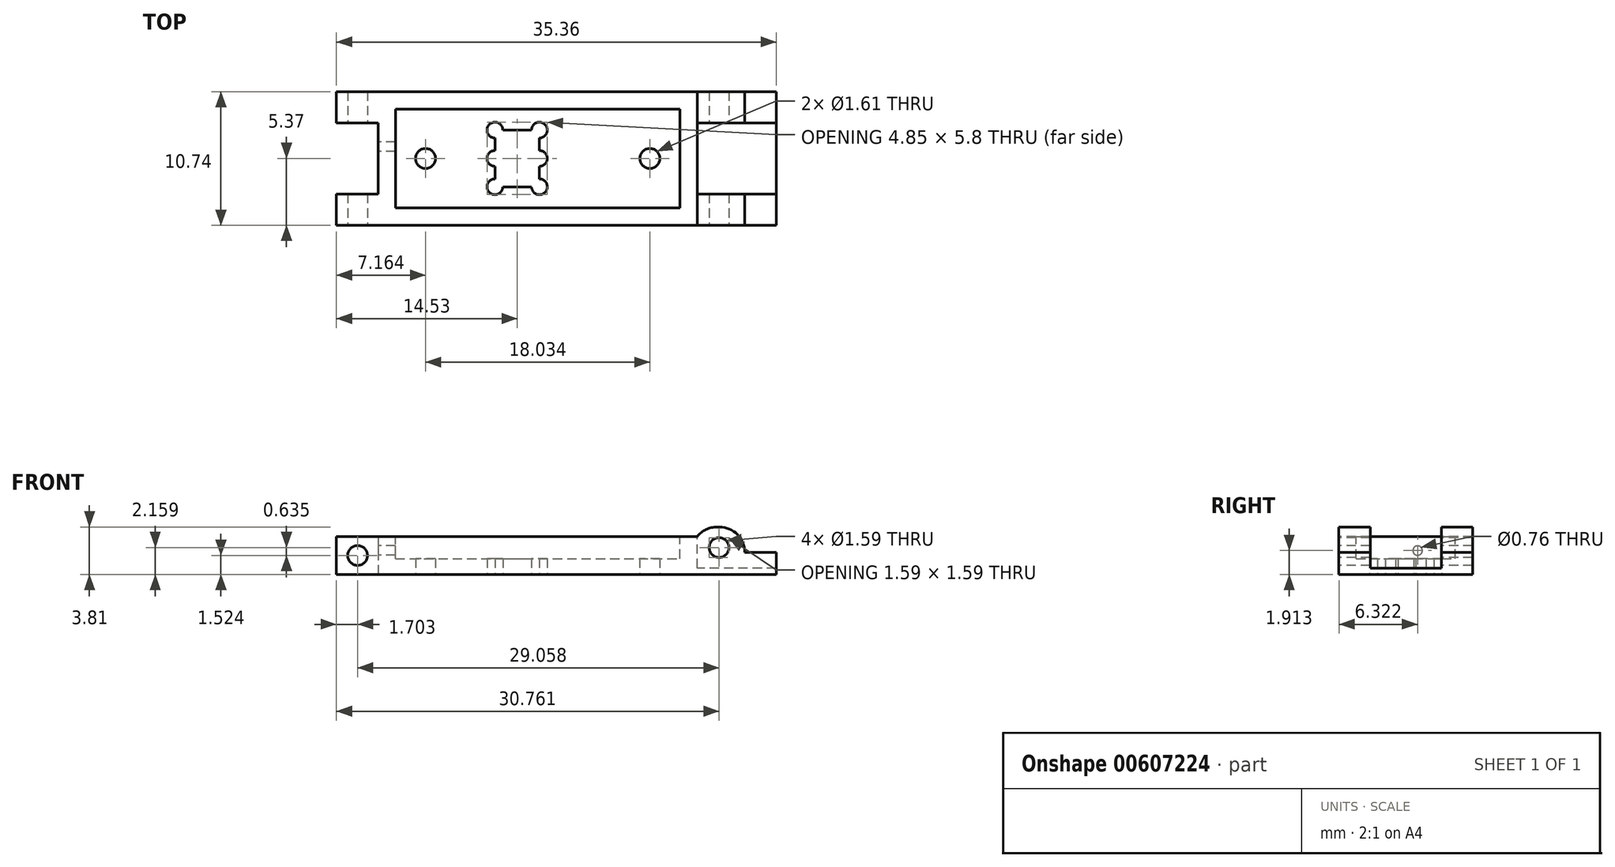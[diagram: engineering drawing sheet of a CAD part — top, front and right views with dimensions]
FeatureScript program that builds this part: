
annotation { "Feature Type Name" : "Feature", "Feature Type Description" : "" }
export const myFeature = defineFeature(function(context is Context, id is Id, definition is map)
    precondition{}
    {
        {
            var Q0;
            Q0=qCreatedBy(makeId("Top.planeOp"),FACE);
            var sketch = newSketch(context, id + "F0", { "sketchPlane" : qUnion([Q0])});
            skLineSegment(sketch, "E0.bottom", {"start": v(1.48, 1.88) * mm, "end": v(-1.47, 1.88) * mm, "construction": true});
            skLineSegment(sketch, "E0.top", {"start": v(1.48, -1.88) * mm, "end": v(-1.47, -1.88) * mm, "construction": true});
            skLineSegment(sketch, "E0.left", {"start": v(1.48, 1.88) * mm, "end": v(1.48, -1.88) * mm, "construction": true});
            skLineSegment(sketch, "E0.right", {"start": v(-1.47, 1.88) * mm, "end": v(-1.47, -1.88) * mm, "construction": true});
            skPoint(sketch, "E0.middle", {"position": v(0, 0) * mm});
            skLineSegment(sketch, "E1.bottom", {"start": v(1.79, 2.28) * mm, "end": v(-1.79, 2.28) * mm, "construction": true});
            skLineSegment(sketch, "E1.top", {"start": v(1.79, -2.28) * mm, "end": v(-1.79, -2.28) * mm, "construction": true});
            skLineSegment(sketch, "E2", {"start": v(-1.47, 1.88) * mm, "end": v(-1.79, 2.28) * mm, "construction": true});
            skLineSegment(sketch, "E3", {"start": v(1.79, -2.28) * mm, "end": v(1.48, -1.88) * mm, "construction": true});
            skLineSegment(sketch, "E4", {"start": v(-1.48, 1.88) * mm, "end": v(1.48, -1.88) * mm, "construction": true});
            skArc(sketch, "E5", {"start": v(-1.15, 2.28) * mm, "mid": v(-2.24, 2.73) * mm, "end": v(-1.79, 1.64) * mm});
            skArc(sketch, "E6", {"start": v(1.15, 2.28) * mm, "mid": v(2.24, 2.73) * mm, "end": v(1.79, 1.64) * mm});
            skArc(sketch, "E7", {"start": v(1.79, -1.64) * mm, "mid": v(2.24, -2.73) * mm, "end": v(1.15, -2.28) * mm});
            skArc(sketch, "E8", {"start": v(-1.15, -2.28) * mm, "mid": v(-2.24, -2.73) * mm, "end": v(-1.79, -1.64) * mm});
            skArc(sketch, "E9", {"start": v(-1.79, 0.64) * mm, "mid": v(-2.42, 0) * mm, "end": v(-1.79, -0.64) * mm});
            skArc(sketch, "E10", {"start": v(1.79, 0.64) * mm, "mid": v(2.42, 0) * mm, "end": v(1.79, -0.64) * mm});
            skLineSegment(sketch, "E11", {"start": v(-1.15, 2.28) * mm, "end": v(1.15, 2.28) * mm});
            skLineSegment(sketch, "E12", {"start": v(-1.79, 1.64) * mm, "end": v(-1.79, 0.64) * mm});
            skLineSegment(sketch, "E13", {"start": v(-1.79, -0.64) * mm, "end": v(-1.79, -1.64) * mm});
            skLineSegment(sketch, "E14", {"start": v(-1.15, -2.28) * mm, "end": v(1.15, -2.28) * mm});
            skLineSegment(sketch, "E15", {"start": v(1.79, -1.64) * mm, "end": v(1.79, -0.64) * mm});
            skLineSegment(sketch, "E16", {"start": v(1.79, 0.64) * mm, "end": v(1.79, 1.64) * mm});
            skLineSegment(sketch, "E17", {"start": v(-1.79, 2.28) * mm, "end": v(-1.79, -2.28) * mm, "construction": true});
            skLineSegment(sketch, "E18", {"start": v(1.79, 2.28) * mm, "end": v(1.79, -2.28) * mm, "construction": true});
            skLineSegment(sketch, "E19", {"start": v(20.83, 5.37) * mm, "end": v(20.83, -5.37) * mm});
            skCircle(sketch, "E20", {"center": v(-7.37, 0) * mm, "radius": 0.8 * mm});
            skCircle(sketch, "E21", {"center": v(10.67, 0) * mm, "radius": 0.8 * mm});
            skLineSegment(sketch, "E22.bottom", {"start": v(-11.18, 5.37) * mm, "end": v(-14.53, 5.37) * mm});
            skLineSegment(sketch, "E22.top", {"start": v(-11.18, 2.86) * mm, "end": v(-14.53, 2.86) * mm});
            skLineSegment(sketch, "E22.left", {"start": v(-11.18, 5.37) * mm, "end": v(-11.18, 2.86) * mm});
            skLineSegment(sketch, "E22.right", {"start": v(-14.53, 5.37) * mm, "end": v(-14.53, 2.86) * mm});
            skLineSegment(sketch, "E23.bottom", {"start": v(-11.18, -5.37) * mm, "end": v(-14.53, -5.37) * mm});
            skLineSegment(sketch, "E23.top", {"start": v(-11.18, -2.86) * mm, "end": v(-14.53, -2.86) * mm});
            skLineSegment(sketch, "E23.left", {"start": v(-11.18, -5.37) * mm, "end": v(-11.18, -2.86) * mm});
            skLineSegment(sketch, "E23.right", {"start": v(-14.53, -5.37) * mm, "end": v(-14.53, -2.86) * mm});
            skLineSegment(sketch, "E24.bottom", {"start": v(-11.18, -5.37) * mm, "end": v(14.48, -5.37) * mm});
            skLineSegment(sketch, "E24.top", {"start": v(-11.18, 5.37) * mm, "end": v(14.48, 5.37) * mm});
            skLineSegment(sketch, "E24.left", {"start": v(-11.18, -5.37) * mm, "end": v(-11.18, 5.37) * mm});
            skLineSegment(sketch, "E24.right", {"start": v(14.48, -5.37) * mm, "end": v(14.48, 5.37) * mm});
            skLineSegment(sketch, "E25.bottom", {"start": v(14.48, 5.37) * mm, "end": v(20.83, 5.37) * mm});
            skLineSegment(sketch, "E25.top", {"start": v(14.48, -5.37) * mm, "end": v(20.83, -5.37) * mm});
            skLineSegment(sketch, "E25.left", {"start": v(14.48, 5.37) * mm, "end": v(14.48, -5.37) * mm, "construction": true});
            skLineSegment(sketch, "E26", {"start": v(20.83, 0) * mm, "end": v(14.48, 0) * mm, "construction": true});
            skSolve(sketch);
        }
        {
            var Q0;
            Q0=makeQuery(id+"F0.imprint","IMPRINT",FACE,{"disambiguationData":[TD([[makeQuery(id+"F0.imprint","IMPRINT",EDGE,{"derivedFrom":sQuery(id+"F0.wireOp",EDGE,"E22.bottom")}),1.0]])]});
            var Q1;
            Q1=makeQuery(id+"F0.imprint","IMPRINT",FACE,{"disambiguationData":[TD([[makeQuery(id+"F0.imprint","IMPRINT",EDGE,{"derivedFrom":sQuery(id+"F0.wireOp",EDGE,"E23.bottom")}),-1.0]])]});
            var Q2;
            Q2=makeQuery(id+"F0.imprint","IMPRINT",FACE,{"disambiguationData":[TD([[makeQuery(id+"F0.imprint","IMPRINT",EDGE,{"derivedFrom":sQuery(id+"F0.wireOp",EDGE,"E5")}),-1.0]])]});
            var Q3;
            Q3=makeQuery(id+"F0.imprint","IMPRINT",FACE,{"disambiguationData":[TD([[makeQuery(id+"F0.imprint","IMPRINT",EDGE,{"derivedFrom":sQuery(id+"F0.wireOp",EDGE,"E24.right")}),-1.0]])]});
            extrude(context, id + "F1", {"entities" : qUnion([Q0, Q1, Q2, Q3]), "depth" : 3.05 * mm, "offsetDistance" : 25.4 * mm});
        }
        {
            var Q0;
            Q0=makeQuery(id+"F1.opExtrude","CAP_FACE",FACE,{"disambiguationData":[OSD([sQuery(id+"F0.wireOp",EDGE,"E5"),sQuery(id+"F0.wireOp",EDGE,"E6"),sQuery(id+"F0.wireOp",EDGE,"E7"),sQuery(id+"F0.wireOp",EDGE,"E8"),sQuery(id+"F0.wireOp",EDGE,"E9"),sQuery(id+"F0.wireOp",EDGE,"E10"),sQuery(id+"F0.wireOp",EDGE,"E11"),sQuery(id+"F0.wireOp",EDGE,"E12"),sQuery(id+"F0.wireOp",EDGE,"E13"),sQuery(id+"F0.wireOp",EDGE,"E14"),sQuery(id+"F0.wireOp",EDGE,"E15"),sQuery(id+"F0.wireOp",EDGE,"E16"),sQuery(id+"F0.wireOp",EDGE,"HfviohbY-Hr04-ZRmY-4y10-KckNNT6P6HvO.bottom"),sQuery(id+"F0.wireOp",EDGE,"HfviohbY-Hr04-ZRmY-4y10-KckNNT6P6HvO.top"),sQuery(id+"F0.wireOp",EDGE,"HfviohbY-Hr04-ZRmY-4y10-KckNNT6P6HvO.left"),sQuery(id+"F0.wireOp",EDGE,"HfviohbY-Hr04-ZRmY-4y10-KckNNT6P6HvO.right")])],"isStart":false});
            var sketch = newSketch(context, id + "F2", { "sketchPlane" : qUnion([Q0])});
            skLineSegment(sketch, "E27.bottom", {"start": v(20.83, 5.37) * mm, "end": v(18.29, 5.37) * mm});
            skLineSegment(sketch, "E27.top", {"start": v(20.83, -5.37) * mm, "end": v(18.29, -5.37) * mm});
            skLineSegment(sketch, "E27.left", {"start": v(20.83, 5.37) * mm, "end": v(20.83, -5.37) * mm});
            skLineSegment(sketch, "E27.right", {"start": v(18.29, 5.37) * mm, "end": v(18.29, -5.37) * mm});
            skCircle(sketch, "E28", {"center": v(-7.37, 0) * mm, "radius": 1.47 * mm, "construction": true});
            skCircle(sketch, "E29", {"center": v(10.67, 0) * mm, "radius": 1.47 * mm, "construction": true});
            skLineSegment(sketch, "E30", {"start": v(-11.18, 0) * mm, "end": v(-9.78, 0) * mm, "construction": true});
            skLineSegment(sketch, "E31", {"start": v(0, -5.37) * mm, "end": v(0, -3.98) * mm, "construction": true});
            skPoint(sketch, "E32.middle", {"position": v(0, 0) * mm});
            skLineSegment(sketch, "E33.bottom", {"start": v(-9.78, -3.98) * mm, "end": v(13.08, -3.98) * mm});
            skLineSegment(sketch, "E33.top", {"start": v(-9.78, 3.98) * mm, "end": v(13.08, 3.98) * mm});
            skLineSegment(sketch, "E33.left", {"start": v(-9.78, -3.98) * mm, "end": v(-9.78, 3.98) * mm});
            skLineSegment(sketch, "E33.right", {"start": v(13.08, -3.98) * mm, "end": v(13.08, 3.98) * mm});
            skLineSegment(sketch, "E34", {"start": v(-9.78, 0) * mm, "end": v(-8.84, 0) * mm, "construction": true});
            skLineSegment(sketch, "E35", {"start": v(13.08, 0) * mm, "end": v(12.14, 0) * mm, "construction": true});
            skSolve(sketch);
        }
        {
            var Q0;
            Q0=qSketchRegion(id+"F2",true);
            extrude(context, id + "F3", {"entities" : qUnion([Q0]), "operationType" : NewBodyOperationType.REMOVE, "oppositeDirection" : true, "depth" : 1.27 * mm, "offsetDistance" : 25.4 * mm});
        }
        {
            var Q0;
            Q0=makeQuery(id+"F1.opExtrude","CAP_FACE",FACE,{"disambiguationData":[OSD([sQuery(id+"F0.wireOp",EDGE,"E5"),sQuery(id+"F0.wireOp",EDGE,"E6"),sQuery(id+"F0.wireOp",EDGE,"E7"),sQuery(id+"F0.wireOp",EDGE,"E8"),sQuery(id+"F0.wireOp",EDGE,"E9"),sQuery(id+"F0.wireOp",EDGE,"E10"),sQuery(id+"F0.wireOp",EDGE,"E11"),sQuery(id+"F0.wireOp",EDGE,"E12"),sQuery(id+"F0.wireOp",EDGE,"E13"),sQuery(id+"F0.wireOp",EDGE,"E14"),sQuery(id+"F0.wireOp",EDGE,"E15"),sQuery(id+"F0.wireOp",EDGE,"E16"),sQuery(id+"F0.wireOp",EDGE,"HfviohbY-Hr04-ZRmY-4y10-KckNNT6P6HvO.bottom"),sQuery(id+"F0.wireOp",EDGE,"HfviohbY-Hr04-ZRmY-4y10-KckNNT6P6HvO.top"),sQuery(id+"F0.wireOp",EDGE,"HfviohbY-Hr04-ZRmY-4y10-KckNNT6P6HvO.left"),sQuery(id+"F0.wireOp",EDGE,"YcC6wYwr-SVXZ-vRu8-w98k-MYfRG6CX6vEh"),sQuery(id+"F0.wireOp",EDGE,"E19"),sQuery(id+"F0.wireOp",EDGE,"X6KMa0kz-Fo9u-lM4c-e0Po-d6rj0lJBtCXR"),sQuery(id+"F0.wireOp",EDGE,"E20"),sQuery(id+"F0.wireOp",EDGE,"E21"),sQuery(id+"F0.wireOp",EDGE,"E22.bottom"),sQuery(id+"F0.wireOp",EDGE,"E22.top"),sQuery(id+"F0.wireOp",EDGE,"E22.right"),sQuery(id+"F0.wireOp",EDGE,"E23.bottom"),sQuery(id+"F0.wireOp",EDGE,"E23.top"),sQuery(id+"F0.wireOp",EDGE,"E23.right")])],"isStart":false});
            var sketch = newSketch(context, id + "F4", { "sketchPlane" : qUnion([Q0])});
            skLineSegment(sketch, "E36.0", {"start": v(20.83, 5.37) * mm, "end": v(20.83, -5.37) * mm, "construction": true});
            skLineSegment(sketch, "E37.bottom", {"start": v(20.83, -2.86) * mm, "end": v(14.48, -2.86) * mm});
            skLineSegment(sketch, "E37.top", {"start": v(20.83, 2.86) * mm, "end": v(14.48, 2.86) * mm});
            skLineSegment(sketch, "E37.left", {"start": v(20.83, -2.86) * mm, "end": v(20.83, 2.86) * mm});
            skLineSegment(sketch, "E37.right", {"start": v(14.48, -2.86) * mm, "end": v(14.48, 2.86) * mm});
            skLineSegment(sketch, "E38", {"start": v(-11.18, 2.86) * mm, "end": v(14.48, 2.86) * mm, "construction": true});
            skLineSegment(sketch, "E39", {"start": v(14.48, -2.86) * mm, "end": v(-11.18, -2.86) * mm, "construction": true});
            skSolve(sketch);
        }
        {
            var Q0;
            Q0=qSketchRegion(id+"F4",true);
            extrude(context, id + "F5", {"entities" : qUnion([Q0]), "operationType" : NewBodyOperationType.REMOVE, "oppositeDirection" : true, "depth" : 2.54 * mm, "offsetDistance" : 25.4 * mm});
        }
        {
            var Q0;
            Q0=makeQuery(id+"F1.opExtrude","SWEPT_FACE",FACE,{"disambiguationData":[OSD([sQuery(id+"F0.wireOp",EDGE,"HfviohbY-Hr04-ZRmY-4y10-KckNNT6P6HvO.top"),sQuery(id+"F0.wireOp",EDGE,"X6KMa0kz-Fo9u-lM4c-e0Po-d6rj0lJBtCXR"),sQuery(id+"F0.wireOp",EDGE,"E23.bottom")])]});
            var sketch = newSketch(context, id + "F6", { "sketchPlane" : qUnion([Q0])});
            skCircle(sketch, "E40", {"center": v(-12.83, 1.52) * mm, "radius": 0.8 * mm});
            skCircle(sketch, "E41", {"center": v(16.23, 2.16) * mm, "radius": 0.8 * mm});
            skLineSegment(sketch, "E42", {"start": v(-12.83, 3.05) * mm, "end": v(-12.83, 0) * mm, "construction": true});
            skLineSegment(sketch, "E43.0", {"start": v(18.29, 3.05) * mm, "end": v(14.48, 3.05) * mm, "construction": true});
            skSolve(sketch);
        }
        {
            var Q0;
            Q0=qSketchRegion(id+"F6",true);
            extrude(context, id + "F7", {"entities" : qUnion([Q0]), "operationType" : NewBodyOperationType.REMOVE, "endBound" : BoundingType.THROUGH_ALL, "oppositeDirection" : true, "depth" : 25.4 * mm, "offsetDistance" : 25.4 * mm});
        }
        {
            var Q0;
            Q0=makeQuery(id+"F3.boolean.opBoolean","COPY",FACE,{"derivedFrom":makeQuery(id+"F3.opExtrude","CAP_FACE",FACE,{"disambiguationData":[OSD([sQuery(id+"F2.wireOp",EDGE,"E33.bottom"),sQuery(id+"F2.wireOp",EDGE,"E33.top"),sQuery(id+"F2.wireOp",EDGE,"E33.left"),sQuery(id+"F2.wireOp",EDGE,"E33.right")])],"isStart":false})});
            extrude(context, id + "F8", {"entities" : qUnion([Q0]), "operationType" : NewBodyOperationType.REMOVE, "oppositeDirection" : true, "depth" : 0.5 * mm, "offsetDistance" : 25.4 * mm});
        }
        {
            var Q0;
            Q0=makeQuery(id+"F1.opExtrude","CAP_FACE",FACE,{"disambiguationData":[OSD([sQuery(id+"F0.wireOp",EDGE,"E5"),sQuery(id+"F0.wireOp",EDGE,"E6"),sQuery(id+"F0.wireOp",EDGE,"E7"),sQuery(id+"F0.wireOp",EDGE,"E8"),sQuery(id+"F0.wireOp",EDGE,"E9"),sQuery(id+"F0.wireOp",EDGE,"E10"),sQuery(id+"F0.wireOp",EDGE,"E11"),sQuery(id+"F0.wireOp",EDGE,"E12"),sQuery(id+"F0.wireOp",EDGE,"E13"),sQuery(id+"F0.wireOp",EDGE,"E14"),sQuery(id+"F0.wireOp",EDGE,"E15"),sQuery(id+"F0.wireOp",EDGE,"E16"),sQuery(id+"F0.wireOp",EDGE,"HfviohbY-Hr04-ZRmY-4y10-KckNNT6P6HvO.bottom"),sQuery(id+"F0.wireOp",EDGE,"HfviohbY-Hr04-ZRmY-4y10-KckNNT6P6HvO.top"),sQuery(id+"F0.wireOp",EDGE,"HfviohbY-Hr04-ZRmY-4y10-KckNNT6P6HvO.left"),sQuery(id+"F0.wireOp",EDGE,"YcC6wYwr-SVXZ-vRu8-w98k-MYfRG6CX6vEh"),sQuery(id+"F0.wireOp",EDGE,"E19"),sQuery(id+"F0.wireOp",EDGE,"X6KMa0kz-Fo9u-lM4c-e0Po-d6rj0lJBtCXR"),sQuery(id+"F0.wireOp",EDGE,"E20"),sQuery(id+"F0.wireOp",EDGE,"E21"),sQuery(id+"F0.wireOp",EDGE,"E22.bottom"),sQuery(id+"F0.wireOp",EDGE,"E22.top"),sQuery(id+"F0.wireOp",EDGE,"E22.right"),sQuery(id+"F0.wireOp",EDGE,"E23.bottom"),sQuery(id+"F0.wireOp",EDGE,"E23.top"),sQuery(id+"F0.wireOp",EDGE,"E23.right")])],"isStart":false});
            var sketch = newSketch(context, id + "F9", { "sketchPlane" : qUnion([Q0])});
            skLineSegment(sketch, "E44.bottom", {"start": v(18.29, 5.37) * mm, "end": v(14.48, 5.37) * mm});
            skLineSegment(sketch, "E44.top", {"start": v(18.29, 2.86) * mm, "end": v(14.48, 2.86) * mm});
            skLineSegment(sketch, "E44.left", {"start": v(18.29, 5.37) * mm, "end": v(18.29, 2.86) * mm});
            skLineSegment(sketch, "E44.right", {"start": v(14.48, 5.37) * mm, "end": v(14.48, 2.86) * mm});
            skLineSegment(sketch, "E45.bottom", {"start": v(18.29, -2.86) * mm, "end": v(14.48, -2.86) * mm});
            skLineSegment(sketch, "E45.top", {"start": v(18.29, -5.37) * mm, "end": v(14.48, -5.37) * mm});
            skLineSegment(sketch, "E45.left", {"start": v(18.29, -2.86) * mm, "end": v(18.29, -5.37) * mm});
            skLineSegment(sketch, "E45.right", {"start": v(14.48, -2.86) * mm, "end": v(14.48, -5.37) * mm});
            skSolve(sketch);
        }
        {
            var Q0;
            Q0=qSketchRegion(id+"F9",true);
            extrude(context, id + "F10", {"entities" : qUnion([Q0]), "operationType" : NewBodyOperationType.ADD, "depth" : 0.76 * mm, "offsetDistance" : 25.4 * mm});
        }
        {
            var Q0;
            Q0=makeQuery(id+"F10.opExtrude","CAP_EDGE",EDGE,{"disambiguationData":[OSD([sQuery(id+"F9.wireOp",EDGE,"E45.right")])],"isStart":false});
            var Q1;
            Q1=makeQuery(id+"F10.opExtrude","CAP_EDGE",EDGE,{"disambiguationData":[OSD([sQuery(id+"F9.wireOp",EDGE,"E44.right")])],"isStart":false});
            var Q2;
            Q2=makeQuery(id+"F10.opExtrude","CAP_EDGE",EDGE,{"disambiguationData":[OSD([sQuery(id+"F9.wireOp",EDGE,"E44.left")])],"isStart":false});
            var Q3;
            Q3=makeQuery(id+"F10.opExtrude","CAP_EDGE",EDGE,{"disambiguationData":[OSD([sQuery(id+"F9.wireOp",EDGE,"E45.left")])],"isStart":false});
            fillet(context, id + "F11", {"entities" : qUnion([Q0, Q1, Q2, Q3]), "radius" : 2.03 * mm, "tangentPropagation" : true, "allowEdgeOverflow" : false});
        }
        {
            var Q0;
            Q0=makeQuery(id+"F1.opExtrude","SWEPT_FACE",FACE,{"disambiguationData":[OSD([sQuery(id+"F0.wireOp",EDGE,"E24.left")])]});
            var sketch = newSketch(context, id + "F12", { "sketchPlane" : qUnion([Q0])});
            skCircle(sketch, "E46", {"center": v(-0.95, 1.91) * mm, "radius": 0.38 * mm});
            skSolve(sketch);
        }
        {
            var Q0;
            Q0=qSketchRegion(id+"F12",true);
            var Q1;
            {var subQ0=sQuery(id+"F2.wireOp",EDGE,"E32.left");Q1=makeQuery(id+"F8.boolean.opBoolean","MERGE",FACE,{"derivedFrom":[makeQuery(id+"F3.boolean.opBoolean","COPY",FACE,{"derivedFrom":makeQuery(id+"F3.opExtrude","SWEPT_FACE",FACE,{"disambiguationData":[OSD([subQ0])]})}),makeQuery(id+"F8.opExtrude","SWEPT_FACE",FACE,{"disambiguationData":[OSD([subQ0])]})]});}
            extrude(context, id + "F13", {"entities" : qUnion([Q0, Q1]), "operationType" : NewBodyOperationType.REMOVE, "endBound" : BoundingType.UP_TO_NEXT, "oppositeDirection" : true, "depth" : 25.4 * mm, "offsetDistance" : 25.4 * mm});
        }
    });
